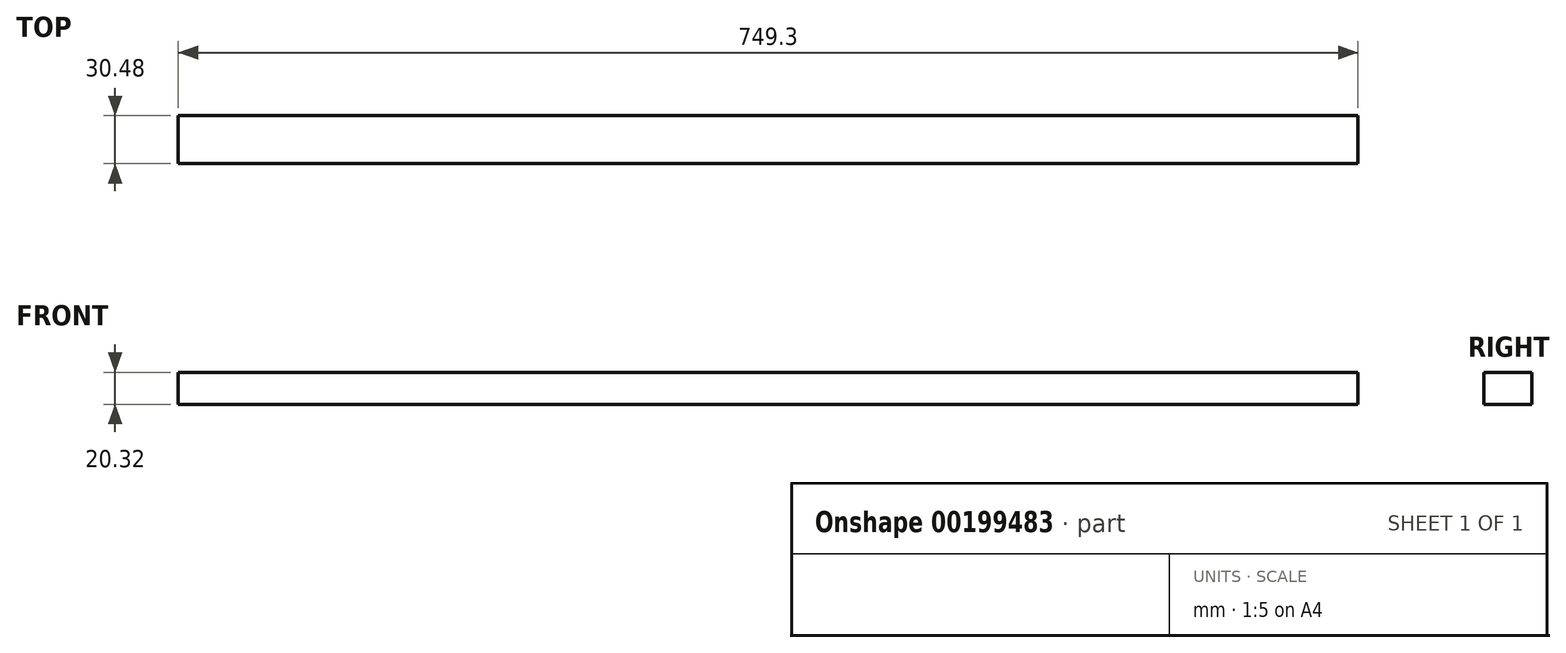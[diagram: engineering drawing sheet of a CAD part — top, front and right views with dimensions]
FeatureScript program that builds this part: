
annotation { "Feature Type Name" : "Feature", "Feature Type Description" : "" }
export const myFeature = defineFeature(function(context is Context, id is Id, definition is map)
    precondition{}
    {
        {
            var Q0;
            Q0=qCreatedBy(makeId("Front.planeOp"),FACE);
            var sketch = newSketch(context, id + "F0", { "sketchPlane" : qUnion([Q0])});
            skLineSegment(sketch, "E0.bottom", {"start": v(-369.87, 0) * mm, "end": v(379.43, 0) * mm});
            skLineSegment(sketch, "E0.top", {"start": v(-369.87, 20.32) * mm, "end": v(379.43, 20.32) * mm});
            skLineSegment(sketch, "E0.left", {"start": v(-369.87, 0) * mm, "end": v(-369.87, 20.32) * mm});
            skLineSegment(sketch, "E0.right", {"start": v(379.43, 0) * mm, "end": v(379.43, 20.32) * mm});
            skSolve(sketch);
        }
        {
            var Q0;
            Q0=makeQuery(id+"F0.imprint","IMPRINT",FACE,{"disambiguationData":[TD([[makeQuery(id+"F0.imprint","IMPRINT",EDGE,{"derivedFrom":sQuery(id+"F0.wireOp",EDGE,"E0.bottom")}),1.0]])]});
            extrude(context, id + "F1", {"entities" : qUnion([Q0]), "depth" : 30.48 * mm});
        }
    });
